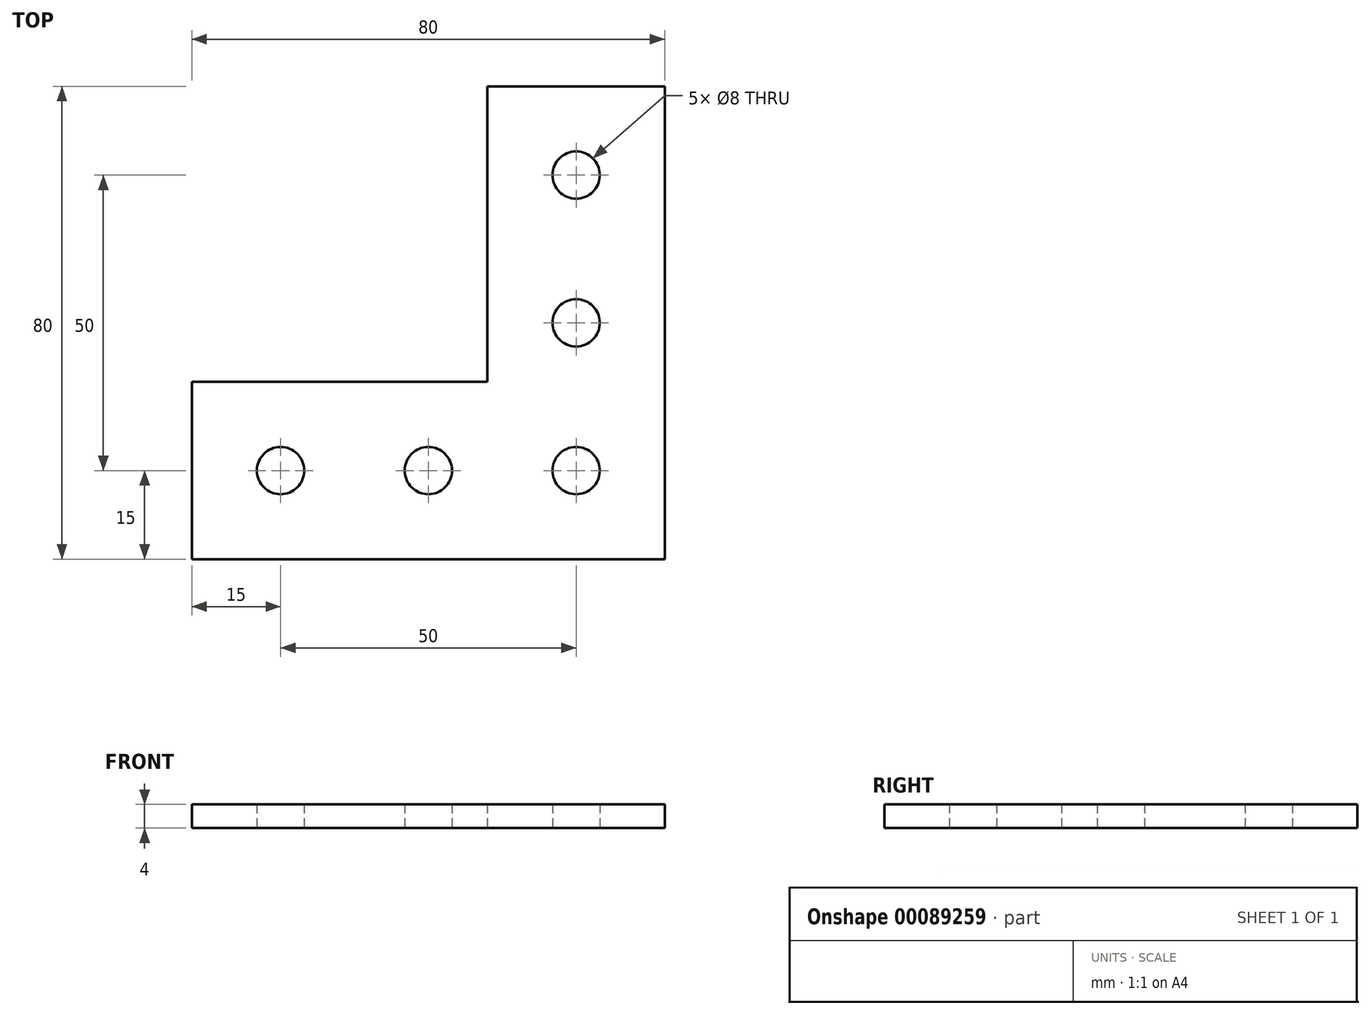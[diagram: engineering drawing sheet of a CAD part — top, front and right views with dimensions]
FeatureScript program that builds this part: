
annotation { "Feature Type Name" : "Feature", "Feature Type Description" : "" }
export const myFeature = defineFeature(function(context is Context, id is Id, definition is map)
    precondition{}
    {
        {
            var Q0;
            Q0=qCreatedBy(makeId("Top.planeOp"),FACE);
            var sketch = newSketch(context, id + "F0", { "sketchPlane" : qUnion([Q0])});
            skLineSegment(sketch, "E0.bottom", {"start": v(10, 40) * mm, "end": v(40, 40) * mm});
            skLineSegment(sketch, "E0.top", {"start": v(-40, -40) * mm, "end": v(40, -40) * mm});
            skLineSegment(sketch, "E0.left", {"start": v(-40, -10) * mm, "end": v(-40, -40) * mm});
            skLineSegment(sketch, "E0.right", {"start": v(40, 40) * mm, "end": v(40, -40) * mm});
            skPoint(sketch, "E0.middle", {"position": v(0, 0) * mm});
            skPoint(sketch, "E1.orphan", {"position": v(-40, 40) * mm});
            skLineSegment(sketch, "E2", {"start": v(-40, -25) * mm, "end": v(40, -25) * mm, "construction": true});
            skLineSegment(sketch, "E3", {"start": v(25, 40) * mm, "end": v(25, -40) * mm, "construction": true});
            skCircle(sketch, "E4", {"center": v(-25, -25) * mm, "radius": 4 * mm});
            skCircle(sketch, "E5", {"center": v(25, -25) * mm, "radius": 4 * mm});
            skCircle(sketch, "E6", {"center": v(25, 0) * mm, "radius": 4 * mm});
            skCircle(sketch, "E7", {"center": v(0, -25) * mm, "radius": 4 * mm});
            skCircle(sketch, "E8", {"center": v(25, 25) * mm, "radius": 4 * mm});
            skLineSegment(sketch, "E9", {"start": v(-25, -25) * mm, "end": v(25, 25) * mm, "construction": true});
            skLineSegment(sketch, "E10", {"start": v(-40, -10) * mm, "end": v(40, -10) * mm, "construction": true});
            skLineSegment(sketch, "E11", {"start": v(10, 40) * mm, "end": v(10, -40) * mm, "construction": true});
            skLineSegment(sketch, "E12", {"start": v(10, -10) * mm, "end": v(-15, 15) * mm, "construction": true});
            skLineSegment(sketch, "E13", {"start": v(-40, -10) * mm, "end": v(10, -10) * mm});
            skLineSegment(sketch, "E14", {"start": v(10, 40) * mm, "end": v(10, -10) * mm});
            skSolve(sketch);
        }
        {
            var Q0;
            Q0=makeQuery(id+"F0.imprint","IMPRINT",FACE,{"disambiguationData":[TD([[makeQuery(id+"F0.imprint","IMPRINT",EDGE,{"derivedFrom":sQuery(id+"F0.wireOp",EDGE,"E0.bottom")}),-1.0]])]});
            extrude(context, id + "F1", {"entities" : qUnion([Q0]), "depth" : 4 * mm});
        }
    });
